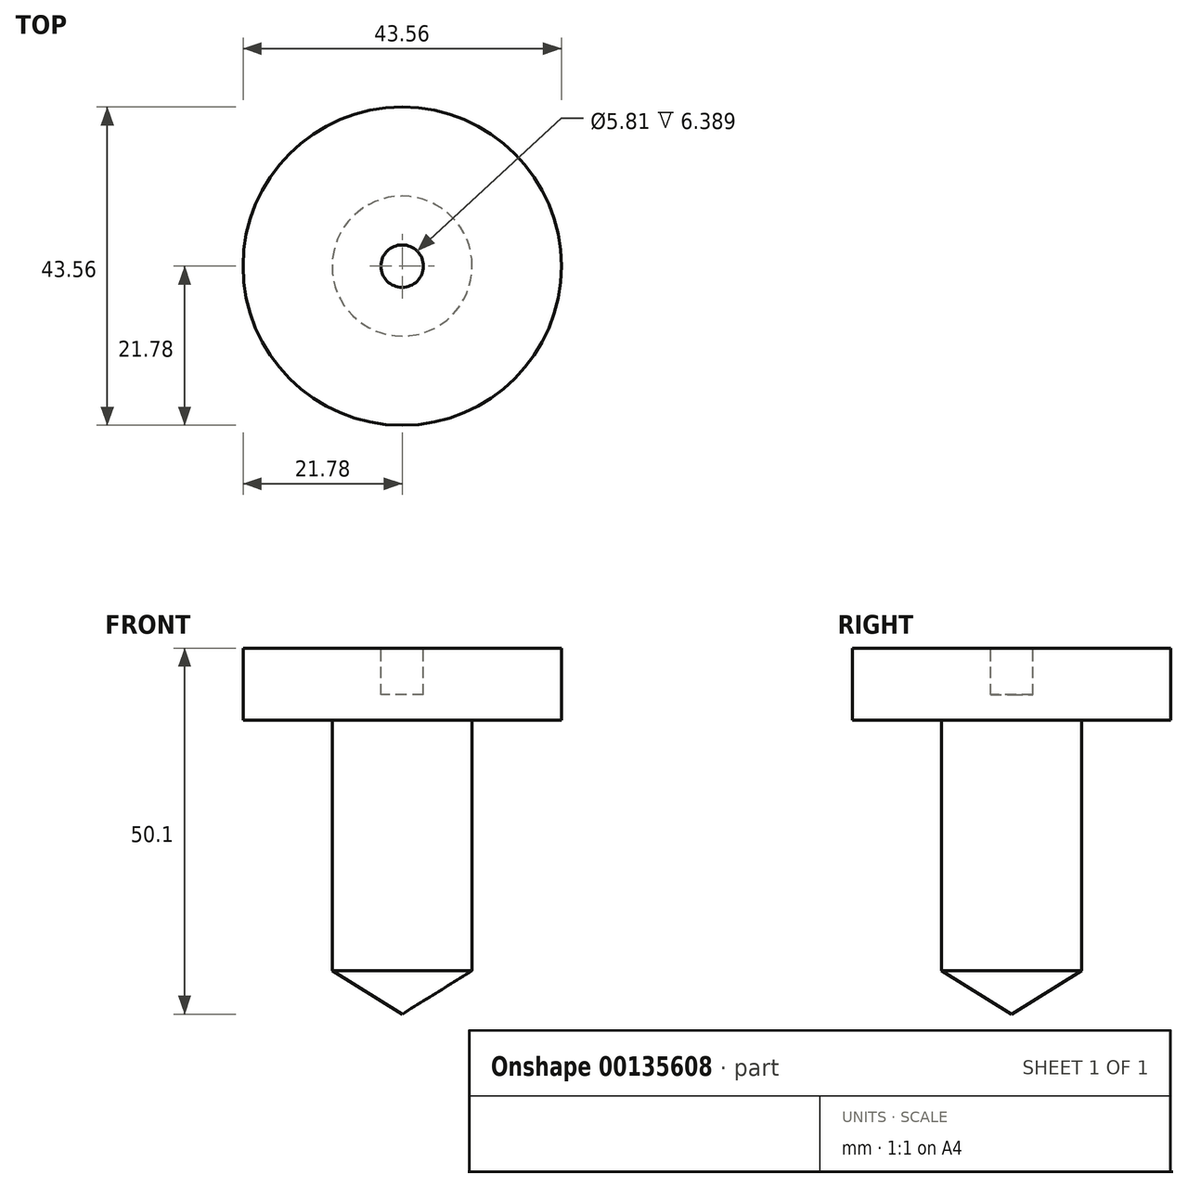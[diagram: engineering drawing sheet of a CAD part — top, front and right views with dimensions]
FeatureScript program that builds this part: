
annotation { "Feature Type Name" : "Feature", "Feature Type Description" : "" }
export const myFeature = defineFeature(function(context is Context, id is Id, definition is map)
    precondition{}
    {
        {
            var Q0;
            Q0=qCreatedBy(makeId("Front.planeOp"),FACE);
            var sketch = newSketch(context, id + "F0", { "sketchPlane" : qUnion([Q0])});
            skLineSegment(sketch, "E0", {"start": v(0, 0) * mm, "end": v(9.58, 5.95) * mm});
            skLineSegment(sketch, "E1", {"start": v(9.58, 5.95) * mm, "end": v(9.58, 40.22) * mm});
            skLineSegment(sketch, "E2", {"start": v(9.58, 40.22) * mm, "end": v(21.78, 40.22) * mm});
            skLineSegment(sketch, "E3", {"start": v(21.78, 40.22) * mm, "end": v(21.78, 50.1) * mm});
            skLineSegment(sketch, "E4", {"start": v(21.78, 50.1) * mm, "end": v(2.9, 50.1) * mm});
            skLineSegment(sketch, "E5", {"start": v(2.9, 50.1) * mm, "end": v(2.9, 43.7) * mm});
            skLineSegment(sketch, "E6", {"start": v(2.9, 43.7) * mm, "end": v(0, 43.7) * mm});
            skLineSegment(sketch, "E7", {"start": v(0, 43.7) * mm, "end": v(0, 0) * mm});
            skSolve(sketch);
        }
        {
            var Q0;
            Q0 = qSketchRegion(id + "F0", true);
            var Q1;
            Q1=makeQuery(id+"F0.imprint","IMPRINT",FACE,{"disambiguationData":[TD([[makeQuery(id+"F0.imprint","IMPRINT",EDGE,{"derivedFrom":sQuery(id+"F0.wireOp",EDGE,"E0")}),1.0]])]});
            var Q2;
            Q2=sQuery(id+"F0.wireOp",EDGE,"E7");
            revolve(context, id + "F1", {"entities" : qUnion([Q0, Q1]), "axis" : qUnion([Q2]), "revolveType" : RevolveType.FULL});
        }
    });
